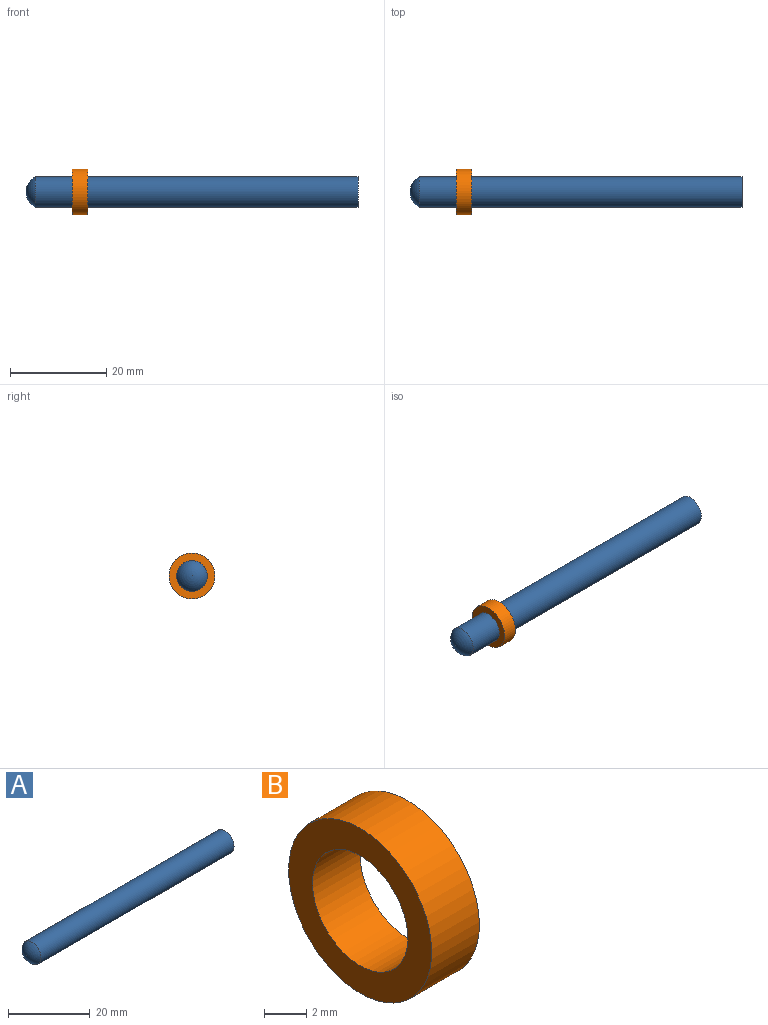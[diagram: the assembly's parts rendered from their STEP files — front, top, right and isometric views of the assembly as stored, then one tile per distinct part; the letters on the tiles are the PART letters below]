
ASSEMBLY  parts=2 mates=1
PART A: 5 faces, bbox 68.8x6.4x6.4 mm
  f0: sphere r=3.57mm, area 43.5mm2, adj f4
  f1: cone r=1.77mm half-angle=72.2deg, axis (1,0,0), area 10.3mm2, adj f2
  f2: cylinder r=1.77mm len=19.05mm, axis (-1,0,0), area 211.3mm2, adj f1,f3
  f3: cone r=1.77mm half-angle=85.2deg, axis (1,0,0), area 22mm2, adj f2,f4
  f4: cylinder r=3.17mm len=66.9mm, axis (-1,0,0), area 1334.5mm2, adj f0,f3
PART B: 4 faces, bbox 3.2x9.5x9.5 mm
  f0: cylinder r=3.17mm len=6.35mm, axis (-1,0,0), area 63.3mm2, adj f2,f3
  f1: cylinder r=4.76mm len=9.53mm, axis (-1,0,0), area 95mm2, adj f2,f3
  f2: plane 9.53x9.53mm, normal (1,0,0), area 39.6mm2, adj f0,f1
  f3: plane 9.53x9.53mm, normal (-1,0,0), area 39.6mm2, adj f0,f1
PLACE A t=(0,0,2.21)mm
PLACE B t=(9.59,0,2.21)mm
MATE slider B.f0 <-> A.f1  axis (-1,0,0) through (12.77,0,2.21)mm
